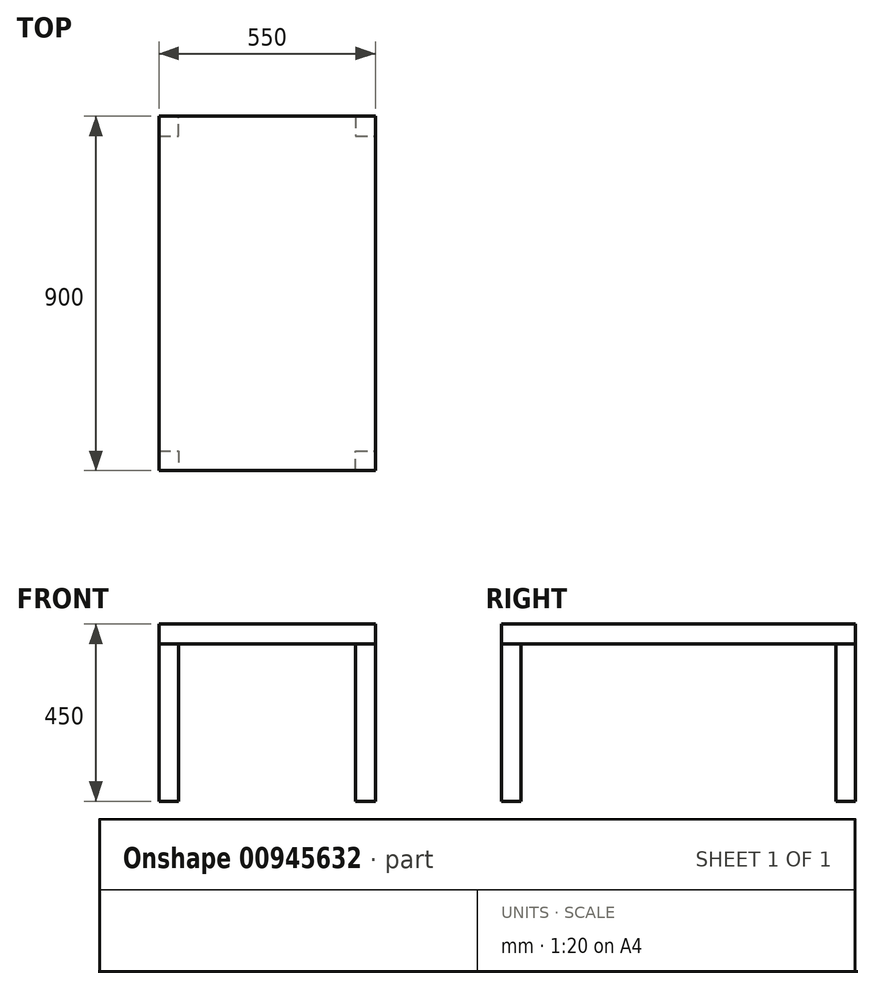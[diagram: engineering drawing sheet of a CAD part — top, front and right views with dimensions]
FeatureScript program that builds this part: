
annotation { "Feature Type Name" : "Feature", "Feature Type Description" : "" }
export const myFeature = defineFeature(function(context is Context, id is Id, definition is map)
    precondition{}
    {
        {
            var Q0;
            Q0=qCreatedBy(makeId("Top.planeOp"),FACE);
            var sketch = newSketch(context, id + "F0", { "sketchPlane" : qUnion([Q0])});
            skLineSegment(sketch, "E0.bottom", {"start": v(275, 450) * mm, "end": v(-275, 450) * mm});
            skLineSegment(sketch, "E0.top", {"start": v(275, -450) * mm, "end": v(-275, -450) * mm});
            skLineSegment(sketch, "E0.left", {"start": v(275, 450) * mm, "end": v(275, -450) * mm});
            skLineSegment(sketch, "E0.right", {"start": v(-275, 450) * mm, "end": v(-275, -450) * mm});
            skPoint(sketch, "E0.middle", {"position": v(0, 0) * mm});
            skSolve(sketch);
        }
        {
            var Q0;
            Q0=makeQuery(id+"F0.imprint","IMPRINT",FACE,{"disambiguationData":[TD([[makeQuery(id+"F0.imprint","IMPRINT",EDGE,{"derivedFrom":sQuery(id+"F0.wireOp",EDGE,"E0.bottom")}),1.0]])]});
            extrude(context, id + "F1", {"entities" : qUnion([Q0]), "depth" : 50 * mm, "offsetDistance" : 25 * mm});
        }
        {
            var Q0;
            Q0=makeQuery(id+"F1.opExtrude","CAP_FACE",FACE,{"disambiguationData":[OSD([sQuery(id+"F0.wireOp",EDGE,"E0.bottom"),sQuery(id+"F0.wireOp",EDGE,"E0.top"),sQuery(id+"F0.wireOp",EDGE,"E0.left"),sQuery(id+"F0.wireOp",EDGE,"E0.right")])],"isStart":true});
            var sketch = newSketch(context, id + "F2", { "sketchPlane" : qUnion([Q0])});
            skLineSegment(sketch, "E1", {"start": v(-275, 400) * mm, "end": v(-225, 400) * mm});
            skLineSegment(sketch, "E2", {"start": v(-225, 400) * mm, "end": v(-225, 450) * mm});
            skLineSegment(sketch, "E3", {"start": v(225, 450) * mm, "end": v(225, 400) * mm});
            skLineSegment(sketch, "E4", {"start": v(225, 400) * mm, "end": v(275, 400) * mm});
            skLineSegment(sketch, "E5", {"start": v(225, -450) * mm, "end": v(225, -400) * mm});
            skLineSegment(sketch, "E6", {"start": v(225, -400) * mm, "end": v(275, -400) * mm});
            skLineSegment(sketch, "E7", {"start": v(-275, -400) * mm, "end": v(-225, -400) * mm});
            skLineSegment(sketch, "E8", {"start": v(-225, -400) * mm, "end": v(-225, -450) * mm});
            skSolve(sketch);
        }
        {
            var Q0;
            Q0 = qSketchRegion(id + "F2", true);
            var Q1;
            {var subQ0=sQuery(id+"F2.wireOp",EDGE,"E1");Q1=makeQuery(id+"F2.imprint","IMPRINT",FACE,{"disambiguationData":[TD([[makeQuery(id+"F2.imprint","IMPRINT",EDGE,{"derivedFrom":subQ0}),1.0]])]});}
            var Q2;
            {var subQ0=sQuery(id+"F2.wireOp",EDGE,"E7");Q2=makeQuery(id+"F2.imprint","IMPRINT",FACE,{"disambiguationData":[TD([[makeQuery(id+"F2.imprint","IMPRINT",EDGE,{"derivedFrom":subQ0}),-1.0]])]});}
            var Q3;
            {var subQ0=sQuery(id+"F2.wireOp",EDGE,"E5");Q3=makeQuery(id+"F2.imprint","IMPRINT",FACE,{"disambiguationData":[TD([[makeQuery(id+"F2.imprint","IMPRINT",EDGE,{"derivedFrom":subQ0}),-1.0]])]});}
            var Q4;
            {var subQ0=sQuery(id+"F2.wireOp",EDGE,"E3");Q4=makeQuery(id+"F2.imprint","IMPRINT",FACE,{"disambiguationData":[TD([[makeQuery(id+"F2.imprint","IMPRINT",EDGE,{"derivedFrom":subQ0}),1.0]])]});}
            extrude(context, id + "F3", {"entities" : qUnion([Q0, Q1, Q2, Q3, Q4]), "depth" : 400 * mm, "offsetDistance" : 25 * mm});
        }
    });
